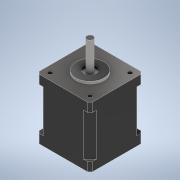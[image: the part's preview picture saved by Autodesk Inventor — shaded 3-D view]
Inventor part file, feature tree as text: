
AUTODESK INVENTOR PART (.ipt)
format: ipt  version: 2021 (Build 250183000, 183)  size: 230,400 bytes
history: native  units: mm
features: extrude x8, sketch x8, chamfer x2
ambient origin geometry x8: Origin, YZ Plane, XZ Plane, XY Plane, X Axis, Y Axis, Z Axis, Center Point
bodies: Solid1 (feature_tree)
feature tree (18):
  extrude  "Extrusion1"  Depth=42.0mm
  chamfer  "Chamfer1"  Distance=47.5mm
  extrude  "Extrusion2"  Depth=7.0mm TaperAngle=0.0deg
  extrude  "Extrusion3"  Depth=2.0mm TaperAngle=45.0deg
  chamfer  "Chamfer2"  Distance=7.0mm
  extrude  "Extrusion4"  Depth=22.0mm
  extrude  "Extrusion5"  Depth=24.0mm
  extrude  "Extrusion6"  Depth=24.0mm
  extrude  "Extrusion7"  Depth=24.0mm
  extrude  "Extrusion8"  Depth=24.0mm
  sketch  "Sketch1"  dims[d0=42.0mm d1=42.0mm d2=47.5mm d3=0.0mm]
  sketch  "Sketch3"  dims[d4=5.0mm d5=2.0mm d6=45.0deg d7=7.0mm d8=0.0mm]
  sketch  "Sketch4"  dims[d9=7.0mm d10=0.0mm d11=2.0mm d12=2.0mm d13=45.0deg]
  sketch  "Sketch5"  dims[d14=10.0mm]
  sketch  "Sketch6"  dims[d15=21.0mm]
  sketch  "Sketch7"  dims[d16=21.0mm d17=7.0mm d18=0.0mm]
  sketch  "Sketch8"  dims[d19=10.0mm d20=22.0mm]
  sketch  "Sketch9"  dims[d21=2.0mm d22=0.0mm d23=3.2mm d24=3.2mm d25=3.2mm d26=3.2mm d27=31.5mm d28=31.5mm d29=31.5mm d30=31.5mm d31=5.25mm d32=5.25mm d33=5.25mm d34=5.25mm d35=10.0mm d36=0.0mm d37=3.2mm d38=3.2mm d39=3.2mm d40=3.2mm d41=2.0mm d42=0.0mm d43=5.0mm d44=21.0mm d45=21.0mm d46=24.0mm d47=0.0mm]
